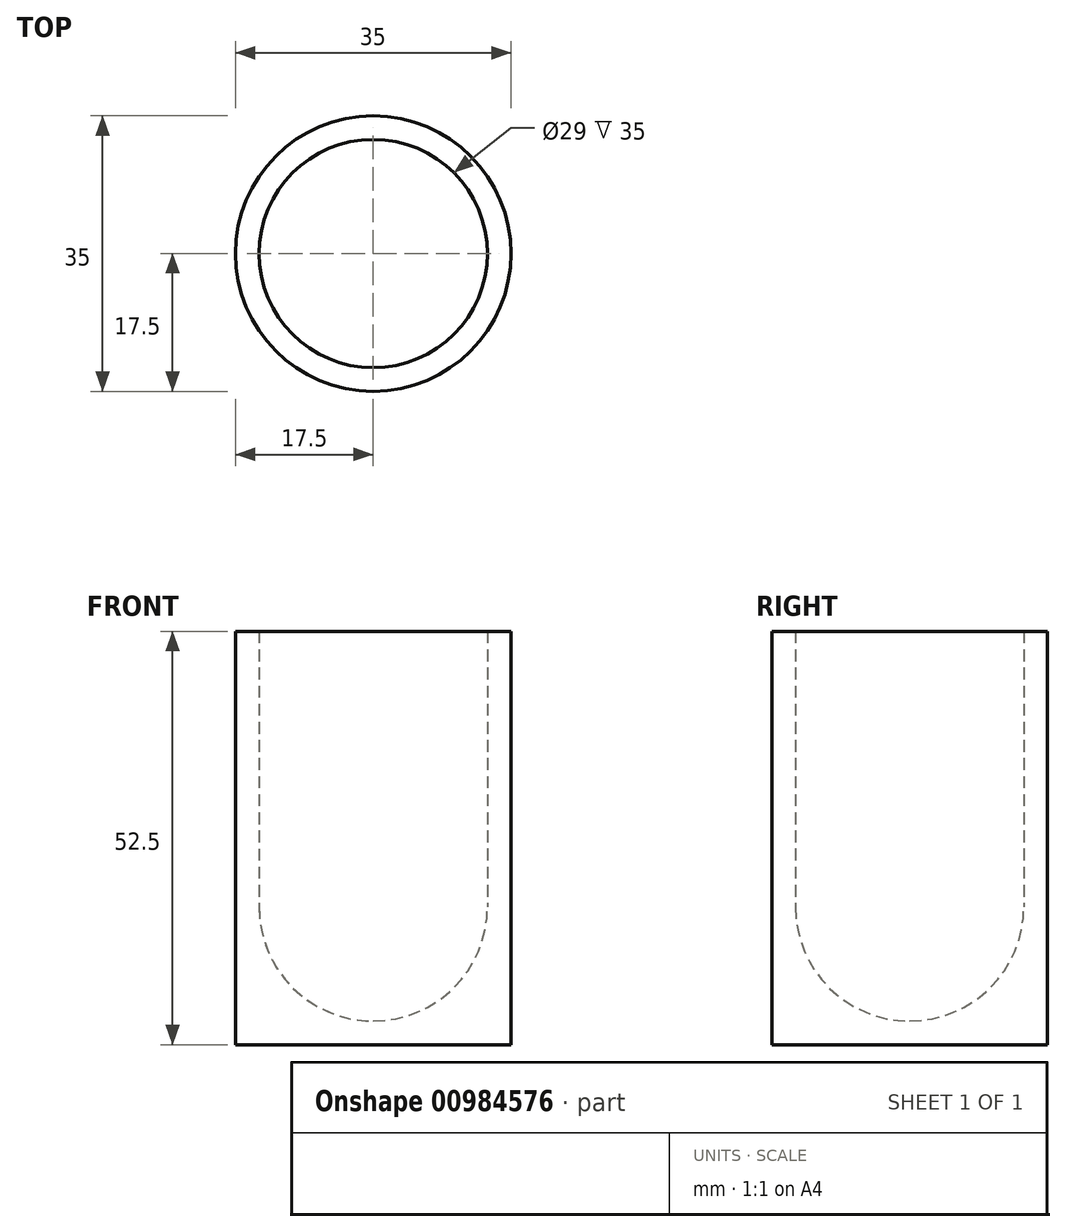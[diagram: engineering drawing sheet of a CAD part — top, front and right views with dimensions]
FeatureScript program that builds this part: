
annotation { "Feature Type Name" : "Feature", "Feature Type Description" : "" }
export const myFeature = defineFeature(function(context is Context, id is Id, definition is map)
    precondition{}
    {
        {
            var Q0;
            Q0=qCreatedBy(makeId("Front.planeOp"),FACE);
            var sketch = newSketch(context, id + "F0", { "sketchPlane" : qUnion([Q0])});
            skPoint(sketch, "E0.middle", {"position": v(0, 0) * mm});
            skLineSegment(sketch, "E1.bottom", {"start": v(-14.5, 17.5) * mm, "end": v(14.5, 17.5) * mm});
            skLineSegment(sketch, "E1.top", {"start": v(-14.5, -17.5) * mm, "end": v(14.5, -17.5) * mm});
            skLineSegment(sketch, "E1.left", {"start": v(-14.5, 17.5) * mm, "end": v(-14.5, -17.5) * mm});
            skLineSegment(sketch, "E1.right", {"start": v(14.5, 17.5) * mm, "end": v(14.5, -17.5) * mm});
            skCircle(sketch, "E2", {"center": v(0, -17.5) * mm, "radius": 14.5 * mm});
            skLineSegment(sketch, "E3.bottom", {"start": v(-17.5, 17.5) * mm, "end": v(17.5, 17.5) * mm});
            skLineSegment(sketch, "E3.top", {"start": v(-17.5, -35) * mm, "end": v(17.5, -35) * mm});
            skLineSegment(sketch, "E3.left", {"start": v(-17.5, 17.5) * mm, "end": v(-17.5, -35) * mm});
            skLineSegment(sketch, "E3.right", {"start": v(17.5, 17.5) * mm, "end": v(17.5, -35) * mm});
            skLineSegment(sketch, "E4", {"start": v(0, -35) * mm, "end": v(0, -32) * mm});
            skSolve(sketch);
        }
        {
            var Q0;
            {var subQ4=sQuery(id+"F0.wireOp",EDGE,"E1.left");Q0=makeQuery(id+"F0.imprint","IMPRINT",FACE,{"disambiguationData":[TD([[makeQuery(id+"F0.imprint","IMPRINT",EDGE,{"derivedFrom":subQ4}),-1.0]])]});}
            var Q1;
            Q1=sQuery(id+"F0.wireOp",EDGE,"E4");
            revolve(context, id + "F1", {"surfaceOperationType" : NewSurfaceOperationType.NEW, "entities" : qUnion([Q0]), "axis" : qUnion([Q1]), "revolveType" : RevolveType.FULL});
        }
    });
